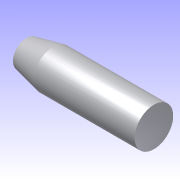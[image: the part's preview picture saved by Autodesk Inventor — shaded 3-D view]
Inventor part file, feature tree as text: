
AUTODESK INVENTOR PART (.ipt)
format: ipt  version: 2012 (Build 160160000, 160)  size: 76,288 bytes
history: native  units: in
note: dims shown in document units (in); Inventor stores cm internally (conversion verified against a paired STEP export)
features: revolve x1, sketch x1
ambient origin geometry x8: Origin, YZ Plane, XZ Plane, XY Plane, X Axis, Y Axis, Z Axis, Center Point
bodies: Solid1 (feature_tree)
feature tree (2):
  revolve  "Revolution1"  [1 undecoded]
  sketch  "Sketch1"  dims[d0=0.7188in d1=1.0in d2=0.5in d3=4.75in d4=90.0deg]
note: 1 required parameter value undecoded (feature->parameter linkage not recoverable at this tier; creation-order binding heuristic only, values carry confidence <= 0.55)
